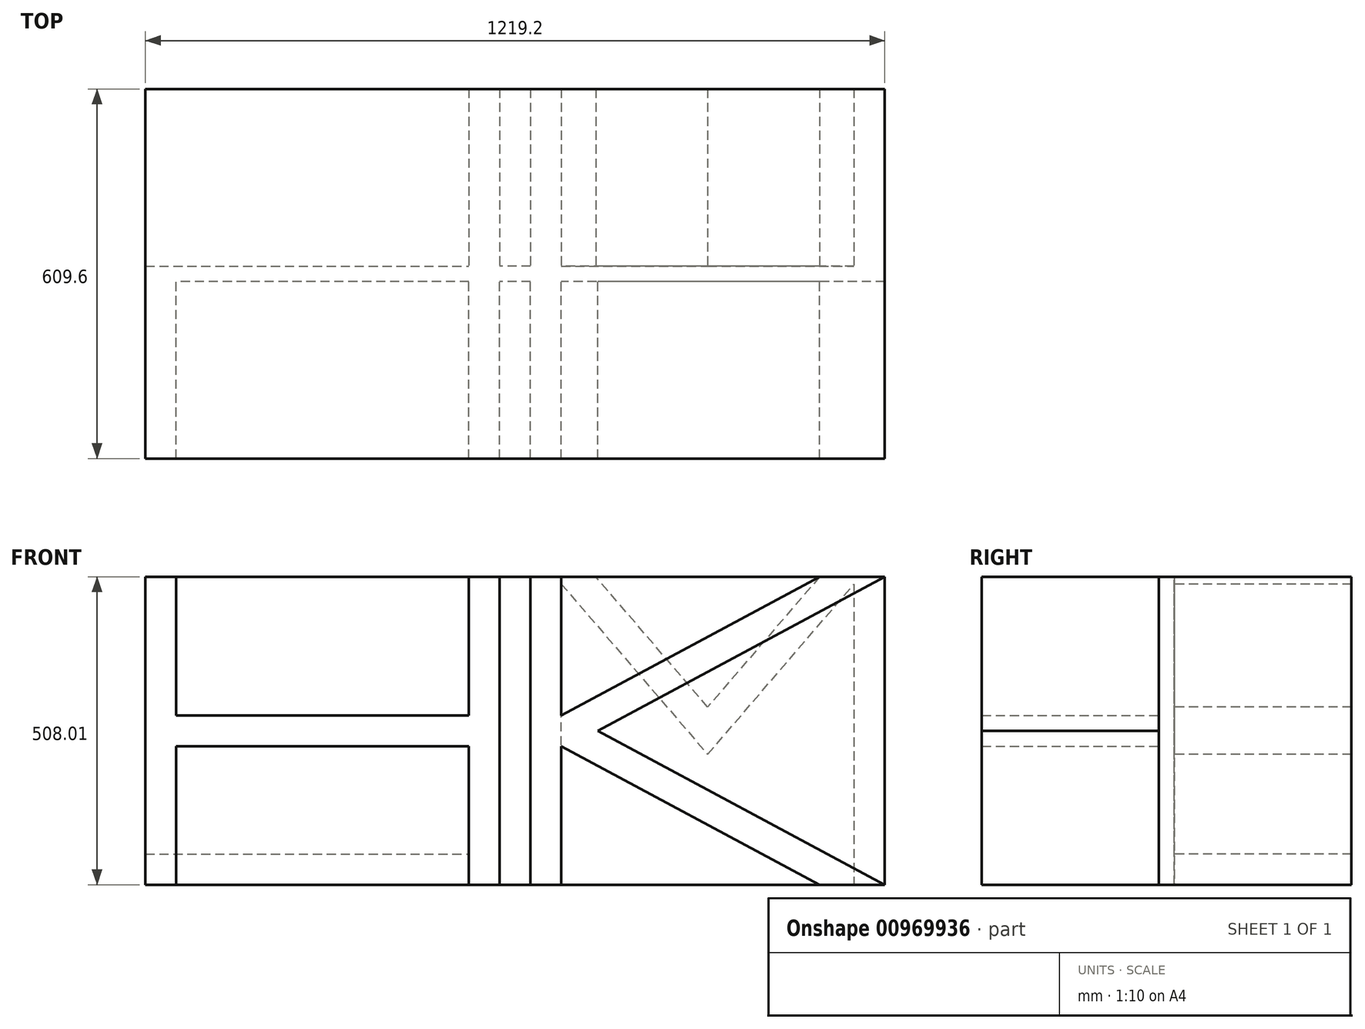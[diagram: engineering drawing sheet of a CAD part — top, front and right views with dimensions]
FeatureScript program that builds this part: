
annotation { "Feature Type Name" : "Feature", "Feature Type Description" : "" }
export const myFeature = defineFeature(function(context is Context, id is Id, definition is map)
    precondition{}
    {
        {
            var Q0;
            Q0=qCreatedBy(makeId("Front.planeOp"),FACE);
            var sketch = newSketch(context, id + "F0", { "sketchPlane" : qUnion([Q0])});
            skLineSegment(sketch, "E0", {"start": v(-609.6, 254) * mm, "end": v(-558.8, 254) * mm});
            skLineSegment(sketch, "E1", {"start": v(-558.8, 254) * mm, "end": v(-558.8, 25.4) * mm});
            skLineSegment(sketch, "E2", {"start": v(-558.8, 25.4) * mm, "end": v(-76.2, 25.4) * mm});
            skLineSegment(sketch, "E3", {"start": v(-76.2, 25.4) * mm, "end": v(-76.2, 254) * mm});
            skLineSegment(sketch, "E4", {"start": v(-76.2, 254) * mm, "end": v(-25.4, 254) * mm});
            skLineSegment(sketch, "E5", {"start": v(-25.4, 254) * mm, "end": v(-25.4, -254) * mm});
            skLineSegment(sketch, "E6", {"start": v(-25.4, -254) * mm, "end": v(-76.2, -254) * mm});
            skLineSegment(sketch, "E7", {"start": v(-76.2, -254) * mm, "end": v(-76.2, -25.4) * mm});
            skLineSegment(sketch, "E8", {"start": v(-76.2, -25.4) * mm, "end": v(-558.8, -25.4) * mm});
            skLineSegment(sketch, "E9", {"start": v(-558.8, -25.4) * mm, "end": v(-558.8, -254) * mm});
            skLineSegment(sketch, "E10", {"start": v(-558.8, -254) * mm, "end": v(-609.6, -254) * mm});
            skLineSegment(sketch, "E11", {"start": v(-609.6, -254) * mm, "end": v(-609.6, 254) * mm});
            skLineSegment(sketch, "E12", {"start": v(25.4, 254) * mm, "end": v(25.4, -254) * mm});
            skLineSegment(sketch, "E13", {"start": v(25.4, -254) * mm, "end": v(76.2, -254) * mm});
            skLineSegment(sketch, "E14", {"start": v(76.2, -254) * mm, "end": v(76.2, -25.4) * mm});
            skLineSegment(sketch, "E15", {"start": v(76.2, -25.4) * mm, "end": v(502.17, -254) * mm});
            skLineSegment(sketch, "E16", {"start": v(502.17, -254) * mm, "end": v(609.6, -254) * mm});
            skLineSegment(sketch, "E17", {"start": v(609.6, -254) * mm, "end": v(136.3, 0) * mm});
            skLineSegment(sketch, "E18", {"start": v(136.3, 0) * mm, "end": v(609.6, 254) * mm});
            skLineSegment(sketch, "E19", {"start": v(609.6, 254) * mm, "end": v(502.17, 254) * mm});
            skLineSegment(sketch, "E20", {"start": v(502.17, 254) * mm, "end": v(76.2, 25.4) * mm});
            skLineSegment(sketch, "E21", {"start": v(76.2, 25.4) * mm, "end": v(76.2, 254) * mm});
            skLineSegment(sketch, "E22", {"start": v(76.2, 254) * mm, "end": v(25.4, 254) * mm});
            skLineSegment(sketch, "E23", {"start": v(-609.6, 0) * mm, "end": v(-25.4, 0) * mm, "construction": true});
            skLineSegment(sketch, "E24", {"start": v(-25.4, 0) * mm, "end": v(25.4, 0) * mm, "construction": true});
            skLineSegment(sketch, "E25", {"start": v(112.28, -44.76) * mm, "end": v(136.3, 0) * mm, "construction": true});
            skLineSegment(sketch, "E26", {"start": v(0, 254) * mm, "end": v(0, -254) * mm, "construction": true});
            skLineSegment(sketch, "E27", {"start": v(25.4, 0) * mm, "end": v(76.2, 0) * mm, "construction": true});
            skLineSegment(sketch, "E28", {"start": v(76.2, 0) * mm, "end": v(136.3, 0) * mm, "construction": true});
            skLineSegment(sketch, "E29", {"start": v(-317.5, 25.4) * mm, "end": v(-317.5, -25.4) * mm, "construction": true});
            skLineSegment(sketch, "E30.bottom", {"start": v(609.6, 254) * mm, "end": v(-609.6, 254) * mm});
            skLineSegment(sketch, "E30.top", {"start": v(609.6, -254) * mm, "end": v(-609.6, -254) * mm});
            skLineSegment(sketch, "E30.left", {"start": v(609.6, 254) * mm, "end": v(609.6, -254) * mm});
            skLineSegment(sketch, "E30.right", {"start": v(-609.6, 254) * mm, "end": v(-609.6, -254) * mm});
            skPoint(sketch, "E30.middle", {"position": v(0, 0) * mm});
            skSolve(sketch);
        }
        {
            var Q0;
            {var subQ0=sQuery(id+"F0.wireOp",EDGE,"E1");Q0=makeQuery(id+"F0.imprint","IMPRINT",FACE,{"disambiguationData":[TD([[makeQuery(id+"F0.imprint","IMPRINT",EDGE,{"derivedFrom":subQ0}),1.0]])]});}
            var Q1;
            {var subQ0=sQuery(id+"F0.wireOp",EDGE,"E7");Q1=makeQuery(id+"F0.imprint","IMPRINT",FACE,{"disambiguationData":[TD([[makeQuery(id+"F0.imprint","IMPRINT",EDGE,{"derivedFrom":subQ0}),1.0]])]});}
            var Q2;
            Q2=makeQuery(id+"F0.imprint","IMPRINT",FACE,{"disambiguationData":[TD([[makeQuery(id+"F0.imprint","IMPRINT",EDGE,{"derivedFrom":sQuery(id+"F0.wireOp",EDGE,"E0")}),-1.0]])]});
            var Q3;
            {var subQ0=sQuery(id+"F0.wireOp",EDGE,"E5");Q3=makeQuery(id+"F0.imprint","IMPRINT",FACE,{"disambiguationData":[TD([[makeQuery(id+"F0.imprint","IMPRINT",EDGE,{"derivedFrom":subQ0}),1.0]])]});}
            var Q4;
            Q4=makeQuery(id+"F0.imprint","IMPRINT",FACE,{"disambiguationData":[TD([[makeQuery(id+"F0.imprint","IMPRINT",EDGE,{"derivedFrom":sQuery(id+"F0.wireOp",EDGE,"E12")}),1.0]])]});
            var Q5;
            {var subQ0=sQuery(id+"F0.wireOp",EDGE,"E14");Q5=makeQuery(id+"F0.imprint","IMPRINT",FACE,{"disambiguationData":[TD([[makeQuery(id+"F0.imprint","IMPRINT",EDGE,{"derivedFrom":subQ0}),-1.0]])]});}
            var Q6;
            Q6=makeQuery(id+"F0.imprint","IMPRINT",FACE,{"disambiguationData":[TD([[makeQuery(id+"F0.imprint","IMPRINT",EDGE,{"derivedFrom":sQuery(id+"F0.wireOp",EDGE,"E17")}),-1.0]])]});
            var Q7;
            {var subQ0=sQuery(id+"F0.wireOp",EDGE,"E20");Q7=makeQuery(id+"F0.imprint","IMPRINT",FACE,{"disambiguationData":[TD([[makeQuery(id+"F0.imprint","IMPRINT",EDGE,{"derivedFrom":subQ0}),-1.0]])]});}
            extrude(context, id + "F1", {"entities" : qUnion([Q0, Q1, Q2, Q3, Q4, Q5, Q6, Q7]), "depth" : 25.4 * mm, "offsetDistance" : 25.4 * mm, "symmetric" : true});
        }
        {
            var Q0;
            Q0=makeQuery(id+"F0.imprint","IMPRINT",FACE,{"disambiguationData":[TD([[makeQuery(id+"F0.imprint","IMPRINT",EDGE,{"derivedFrom":sQuery(id+"F0.wireOp",EDGE,"E0")}),-1.0]])]});
            var Q1;
            Q1=makeQuery(id+"F0.imprint","IMPRINT",FACE,{"disambiguationData":[TD([[makeQuery(id+"F0.imprint","IMPRINT",EDGE,{"derivedFrom":sQuery(id+"F0.wireOp",EDGE,"E12")}),1.0]])]});
            extrude(context, id + "F2", {"entities" : qUnion([Q0, Q1]), "operationType" : NewBodyOperationType.ADD, "depth" : 304.8 * mm, "offsetDistance" : 25.4 * mm});
        }
        {
            var Q0;
            Q0=qCreatedBy(makeId("Front.planeOp"),FACE);
            var sketch = newSketch(context, id + "F3", { "sketchPlane" : qUnion([Q0])});
            skLineSegment(sketch, "E31", {"start": v(25.4, 254) * mm, "end": v(25.4, -254) * mm});
            skLineSegment(sketch, "E32", {"start": v(25.4, -254) * mm, "end": v(76.2, -254) * mm});
            skLineSegment(sketch, "E33", {"start": v(76.2, -254) * mm, "end": v(76.2, 241.97) * mm});
            skLineSegment(sketch, "E34", {"start": v(76.2, 241.97) * mm, "end": v(317.5, -38.98) * mm});
            skLineSegment(sketch, "E35", {"start": v(317.5, -38.98) * mm, "end": v(558.8, 241.97) * mm});
            skLineSegment(sketch, "E36", {"start": v(558.8, 241.97) * mm, "end": v(558.8, -254) * mm});
            skLineSegment(sketch, "E37", {"start": v(558.8, -254) * mm, "end": v(609.6, -254) * mm});
            skLineSegment(sketch, "E38", {"start": v(-25.4, 254) * mm, "end": v(-25.4, -254) * mm});
            skLineSegment(sketch, "E39", {"start": v(-25.4, -254) * mm, "end": v(-609.6, -254) * mm});
            skLineSegment(sketch, "E40", {"start": v(-609.6, -203.2) * mm, "end": v(-76.2, -203.2) * mm});
            skLineSegment(sketch, "E41", {"start": v(-76.2, -203.2) * mm, "end": v(-76.2, 254) * mm});
            skLineSegment(sketch, "E42", {"start": v(-76.2, 254) * mm, "end": v(-25.4, 254) * mm});
            skLineSegment(sketch, "E43", {"start": v(609.6, -254) * mm, "end": v(609.6, 254) * mm});
            skLineSegment(sketch, "E44", {"start": v(-609.6, -203.2) * mm, "end": v(-609.6, -254) * mm});
            skLineSegment(sketch, "E45", {"start": v(25.4, 0) * mm, "end": v(-25.4, 0) * mm, "construction": true});
            skLineSegment(sketch, "E46.0", {"start": v(609.6, 254) * mm, "end": v(502.17, 254) * mm});
            skLineSegment(sketch, "E47", {"start": v(25.4, 254) * mm, "end": v(132.83, 254) * mm});
            skLineSegment(sketch, "E48", {"start": v(502.17, 254) * mm, "end": v(317.5, 38.98) * mm});
            skLineSegment(sketch, "E49", {"start": v(317.5, 38.98) * mm, "end": v(132.83, 254) * mm});
            skLineSegment(sketch, "E50", {"start": v(385.02, 117.6) * mm, "end": v(423.56, 84.5) * mm, "construction": true});
            skLineSegment(sketch, "E51", {"start": v(317.5, 38.98) * mm, "end": v(317.5, -38.98) * mm, "construction": true});
            skPoint(sketch, "E52", {"position": v(317.5, 0) * mm});
            skSolve(sketch);
        }
        {
            var Q0;
            {var subQ0=sQuery(id+"F3.wireOp",EDGE,"E36");Q0=makeQuery(id+"F3.imprint","IMPRINT",FACE,{"disambiguationData":[TD([[makeQuery(id+"F3.imprint","IMPRINT",EDGE,{"derivedFrom":subQ0}),1.0]])]});}
            var Q1;
            {var subQ0=sQuery(id+"F3.wireOp",EDGE,"E31");Q1=makeQuery(id+"F3.imprint","IMPRINT",FACE,{"disambiguationData":[TD([[makeQuery(id+"F3.imprint","IMPRINT",EDGE,{"derivedFrom":subQ0}),1.0]])]});}
            var Q2;
            Q2=makeQuery(id+"F3.imprint","IMPRINT",FACE,{"disambiguationData":[TD([[makeQuery(id+"F3.imprint","IMPRINT",EDGE,{"derivedFrom":sQuery(id+"F3.wireOp",EDGE,"E38")}),-1.0]])]});
            var Q3;
            {var subQ1=sQuery(id+"F3.wireOp",EDGE,"E34");Q3=makeQuery(id+"F3.imprint","IMPRINT",FACE,{"disambiguationData":[TD([[makeQuery(id+"F3.imprint","IMPRINT",EDGE,{"derivedFrom":subQ1}),1.0]])]});}
            extrude(context, id + "F4", {"entities" : qUnion([Q0, Q1, Q2, Q3]), "operationType" : NewBodyOperationType.ADD, "oppositeDirection" : true, "depth" : 304.8 * mm, "offsetDistance" : 25.4 * mm});
        }
        {
            var Q0;
            {var subQ0=sQuery(id+"F0.wireOp",EDGE,"E22");var subQ1=sQuery(id+"F0.wireOp",EDGE,"E19");var subQ2=sQuery(id+"F0.wireOp",EDGE,"E4");var subQ3=sQuery(id+"F0.wireOp",EDGE,"E0");Q0=makeQuery(id+"F4.boolean.opBoolean","MERGE",FACE,{"derivedFrom":[makeQuery(id+"F2.boolean.opBoolean","MERGE",FACE,{"derivedFrom":[makeQuery(id+"F1.opExtrude","SWEPT_FACE",FACE,{"disambiguationData":[OSD([subQ3,subQ2,subQ1,subQ0,sQuery(id+"F0.wireOp",EDGE,"E30.bottom")])]}),makeQuery(id+"F2.opExtrude","SWEPT_FACE",FACE,{"disambiguationData":[OSD([subQ3])]}),makeQuery(id+"F2.opExtrude","SWEPT_FACE",FACE,{"disambiguationData":[OSD([subQ2])]}),makeQuery(id+"F2.opExtrude","SWEPT_FACE",FACE,{"disambiguationData":[OSD([subQ1])]}),makeQuery(id+"F2.opExtrude","SWEPT_FACE",FACE,{"disambiguationData":[OSD([subQ0])]})]}),makeQuery(id+"F4.opExtrude","SWEPT_FACE",FACE,{"disambiguationData":[OSD([sQuery(id+"F3.wireOp",EDGE,"E42")])]}),makeQuery(id+"F4.opExtrude","SWEPT_FACE",FACE,{"disambiguationData":[OSD([sQuery(id+"F3.wireOp",EDGE,"E46.0")])]}),makeQuery(id+"F4.opExtrude","SWEPT_FACE",FACE,{"disambiguationData":[OSD([sQuery(id+"F3.wireOp",EDGE,"E47")])]})]});}
            var sketch = newSketch(context, id + "F5", { "sketchPlane" : qUnion([Q0])});
            skLineSegment(sketch, "E53.bottom", {"start": v(609.6, 304.8) * mm, "end": v(-609.6, 304.8) * mm});
            skLineSegment(sketch, "E53.top", {"start": v(609.6, -304.8) * mm, "end": v(-609.6, -304.8) * mm});
            skLineSegment(sketch, "E53.left", {"start": v(609.6, 304.8) * mm, "end": v(609.6, -304.8) * mm});
            skLineSegment(sketch, "E53.right", {"start": v(-609.6, 304.8) * mm, "end": v(-609.6, -304.8) * mm});
            skPoint(sketch, "E53.middle", {"position": v(0, 0) * mm});
            skSolve(sketch);
        }
        {
            var Q0;
            {var subQ1=sQuery(id+"F0.wireOp",EDGE,"E30.bottom");var subQ2=sQuery(id+"F0.wireOp",EDGE,"E1");var subQ3=sQuery(id+"F0.wireOp",EDGE,"E0");var subQ4=makeQuery(id+"F2.opExtrude","SWEPT_EDGE",EDGE,{"disambiguationData":[OSD([subQ3,subQ2,subQ1])]});Q0=makeQuery(id+"F5.imprint","IMPRINT",FACE,{"disambiguationData":[TD([[makeQuery(id+"F5.imprint","IMPRINT",EDGE,{"derivedFrom":subQ4}),-1.0]])]});}
            var Q1;
            {var subQ1=sQuery(id+"F0.wireOp",EDGE,"E30.bottom");var subQ2=sQuery(id+"F0.wireOp",EDGE,"E20");var subQ3=sQuery(id+"F0.wireOp",EDGE,"E19");var subQ4=makeQuery(id+"F2.opExtrude","SWEPT_EDGE",EDGE,{"disambiguationData":[OSD([subQ3,subQ2,subQ1])]});Q1=makeQuery(id+"F5.imprint","IMPRINT",FACE,{"disambiguationData":[TD([[makeQuery(id+"F5.imprint","IMPRINT",EDGE,{"derivedFrom":subQ4}),1.0]])]});}
            var Q2;
            {var subQ1=sQuery(id+"F0.wireOp",EDGE,"E30.bottom");var subQ2=sQuery(id+"F0.wireOp",EDGE,"E5");var subQ3=sQuery(id+"F0.wireOp",EDGE,"E4");var subQ4=makeQuery(id+"F2.opExtrude","SWEPT_EDGE",EDGE,{"disambiguationData":[OSD([subQ3,subQ2,subQ1])]});Q2=makeQuery(id+"F5.imprint","IMPRINT",FACE,{"disambiguationData":[TD([[makeQuery(id+"F5.imprint","IMPRINT",EDGE,{"derivedFrom":subQ4}),-1.0]])]});}
            var Q3;
            {var subQ36=sQuery(id+"F3.wireOp",EDGE,"E47");var subQ37=sQuery(id+"F3.wireOp",EDGE,"E31");var subQ38=makeQuery(id+"F4.opExtrude","SWEPT_EDGE",EDGE,{"disambiguationData":[OSD([subQ37,subQ36])]});Q3=makeQuery(id+"F5.imprint","IMPRINT",FACE,{"disambiguationData":[TD([[makeQuery(id+"F5.imprint","IMPRINT",EDGE,{"derivedFrom":subQ38}),1.0]])]});}
            var Q4;
            {var subQ1=sQuery(id+"F3.wireOp",EDGE,"E47");var subQ2=sQuery(id+"F3.wireOp",EDGE,"E31");var subQ3=makeQuery(id+"F4.opExtrude","SWEPT_EDGE",EDGE,{"disambiguationData":[OSD([subQ2,subQ1])]});Q4=makeQuery(id+"F5.imprint","IMPRINT",FACE,{"disambiguationData":[TD([[makeQuery(id+"F5.imprint","IMPRINT",EDGE,{"derivedFrom":subQ3}),-1.0]])]});}
            var Q5;
            {var subQ1=sQuery(id+"F3.wireOp",EDGE,"E48");var subQ2=sQuery(id+"F3.wireOp",EDGE,"E46.0");var subQ3=makeQuery(id+"F4.opExtrude","SWEPT_EDGE",EDGE,{"disambiguationData":[OSD([subQ2,subQ1])]});Q5=makeQuery(id+"F5.imprint","IMPRINT",FACE,{"disambiguationData":[TD([[makeQuery(id+"F5.imprint","IMPRINT",EDGE,{"derivedFrom":subQ3}),-1.0]])]});}
            var Q6;
            {var subQ1=sQuery(id+"F3.wireOp",EDGE,"E42");var subQ2=sQuery(id+"F3.wireOp",EDGE,"E41");var subQ3=makeQuery(id+"F4.opExtrude","SWEPT_EDGE",EDGE,{"disambiguationData":[OSD([subQ2,subQ1])]});Q6=makeQuery(id+"F5.imprint","IMPRINT",FACE,{"disambiguationData":[TD([[makeQuery(id+"F5.imprint","IMPRINT",EDGE,{"derivedFrom":subQ3}),-1.0]])]});}
            extrude(context, id + "F6", {"entities" : qUnion([Q0, Q1, Q2, Q3, Q4, Q5, Q6]), "depth" : 3 / 203.2 * mm, "offsetDistance" : 25.4 * mm});
        }
    });
